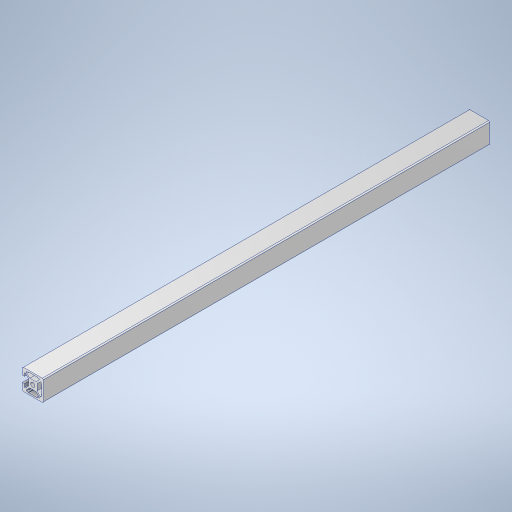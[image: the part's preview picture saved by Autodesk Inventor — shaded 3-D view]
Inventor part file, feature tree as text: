
AUTODESK INVENTOR PART (.ipt)
format: ipt  version: 2024 (Build 280153000, 153)  size: 357,888 bytes
history: native  units: mm
features: other x7, sketch x2, extrude x1, hole x1
ambient origin geometry x8: Origin, YZ Plane, XZ Plane, XY Plane, X Axis, Y Axis, Z Axis, Center Point
bodies: Solid1 (feature_tree)
feature tree (11):
  extrude  "Extrusion1"  TaperAngle=0.0deg  [1 undecoded]
  hole  "Hole1"  [1 undecoded]
  other  "C1_XY"
  other  "C1_YZ"
  other  "C1_ZX"
  other  "C1_X"
  other  "C1_Y"
  other  "C1_Z"
  other  "C1_Center"
  sketch  "Sketch_66"  dims[d2=4.2mm d3=6.0mm d4=4.0mm d5=2.0mm d6=90.0deg d7=425.0mm d8=0.0mm d9=0.0mm]
  sketch  "Sketch2"  dims[d0=425.0mm d1=0.0mm]
note: 2 required parameter values undecoded (feature->parameter linkage not recoverable at this tier; creation-order binding heuristic only, values carry confidence <= 0.55)
